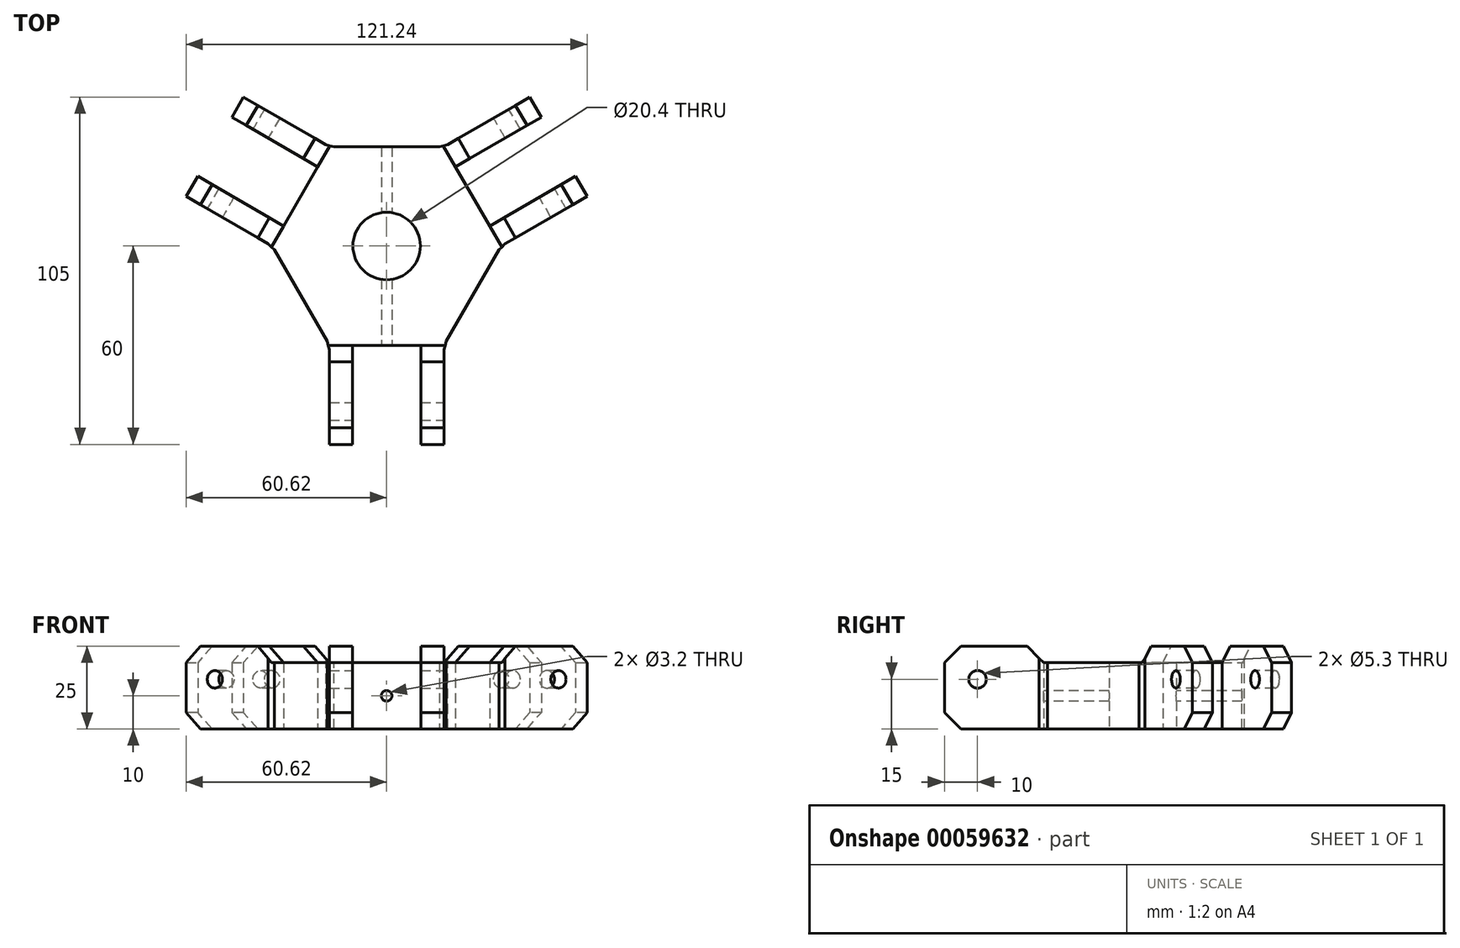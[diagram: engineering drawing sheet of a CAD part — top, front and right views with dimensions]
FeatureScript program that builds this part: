
annotation { "Feature Type Name" : "Feature", "Feature Type Description" : "" }
export const myFeature = defineFeature(function(context is Context, id is Id, definition is map)
    precondition{}
    {
        {
            var Q0;
            Q0=qCreatedBy(makeId("Top.planeOp"),FACE);
            var sketch = newSketch(context, id + "F0", { "sketchPlane" : qUnion([Q0])});
            skLineSegment(sketch, "E0.0", {"start": v(-17.32, 30) * mm, "end": v(17.32, 30) * mm});
            skLineSegment(sketch, "E0.1", {"start": v(17.32, 30) * mm, "end": v(34.64, 0) * mm});
            skLineSegment(sketch, "E0.2", {"start": v(34.64, 0) * mm, "end": v(17.32, -30) * mm});
            skLineSegment(sketch, "E0.3", {"start": v(17.32, -30) * mm, "end": v(-17.32, -30) * mm});
            skLineSegment(sketch, "E0.4", {"start": v(-17.32, -30) * mm, "end": v(-34.64, 0) * mm});
            skLineSegment(sketch, "E0.5", {"start": v(-34.64, 0) * mm, "end": v(-17.32, 30) * mm});
            skLineSegment(sketch, "E1", {"start": v(-34.64, 0) * mm, "end": v(-60.62, 15) * mm});
            skLineSegment(sketch, "E2", {"start": v(-60.62, 15) * mm, "end": v(-57.12, 21.06) * mm});
            skLineSegment(sketch, "E3", {"start": v(-43.3, 45) * mm, "end": v(-17.32, 30) * mm});
            skLineSegment(sketch, "E4", {"start": v(-51.96, 30) * mm, "end": v(-25.98, 15) * mm, "construction": true});
            skLineSegment(sketch, "E5", {"start": v(-46.8, 38.94) * mm, "end": v(-20.82, 23.94) * mm});
            skLineSegment(sketch, "E6", {"start": v(-57.12, 21.06) * mm, "end": v(-31.14, 6.06) * mm});
            skLineSegment(sketch, "E7.trimOffspring", {"start": v(-46.8, 38.94) * mm, "end": v(-43.3, 45) * mm});
            skCircle(sketch, "E8", {"center": v(0, 0) * mm, "radius": 34.64 * mm, "construction": true});
            skLineSegment(sketch, "E9.1.0", {"start": v(10.32, -60) * mm, "end": v(10.32, -30) * mm});
            skLineSegment(sketch, "E9.1.1", {"start": v(-10.32, -60) * mm, "end": v(-17.32, -60) * mm});
            skLineSegment(sketch, "E9.1.2", {"start": v(17.32, -60) * mm, "end": v(10.32, -60) * mm});
            skLineSegment(sketch, "E9.1.3", {"start": v(17.32, -30) * mm, "end": v(17.32, -60) * mm});
            skLineSegment(sketch, "E9.1.4", {"start": v(0, -60) * mm, "end": v(0, -30) * mm, "construction": true});
            skLineSegment(sketch, "E9.1.5", {"start": v(-17.32, -60) * mm, "end": v(-17.32, -30) * mm});
            skLineSegment(sketch, "E9.1.6", {"start": v(-10.32, -60) * mm, "end": v(-10.32, -30) * mm});
            skLineSegment(sketch, "E9.2.0", {"start": v(46.8, 38.94) * mm, "end": v(20.82, 23.94) * mm});
            skLineSegment(sketch, "E9.2.1", {"start": v(57.12, 21.06) * mm, "end": v(60.62, 15) * mm});
            skLineSegment(sketch, "E9.2.2", {"start": v(43.3, 45) * mm, "end": v(46.8, 38.94) * mm});
            skLineSegment(sketch, "E9.2.3", {"start": v(17.32, 30) * mm, "end": v(43.3, 45) * mm});
            skLineSegment(sketch, "E9.2.4", {"start": v(51.96, 30) * mm, "end": v(25.98, 15) * mm, "construction": true});
            skLineSegment(sketch, "E9.2.5", {"start": v(60.62, 15) * mm, "end": v(34.64, 0) * mm});
            skLineSegment(sketch, "E9.2.6", {"start": v(57.12, 21.06) * mm, "end": v(31.14, 6.06) * mm});
            skCircle(sketch, "E10", {"center": v(0, 0) * mm, "radius": 10.2 * mm});
            skSolve(sketch);
        }
        {
            var Q0;
            Q0=makeQuery(id+"F2.opExtrude","CAP_FACE",FACE,{"disambiguationData":[OSD([sQuery(id+"F0.wireOp",EDGE,"E0.0"),sQuery(id+"F0.wireOp",EDGE,"E0.1"),sQuery(id+"F0.wireOp",EDGE,"E0.2"),sQuery(id+"F0.wireOp",EDGE,"E0.3"),sQuery(id+"F0.wireOp",EDGE,"E0.4"),sQuery(id+"F0.wireOp",EDGE,"E0.5"),sQuery(id+"F0.wireOp",EDGE,"E1"),sQuery(id+"F0.wireOp",EDGE,"E2"),sQuery(id+"F0.wireOp",EDGE,"E3"),sQuery(id+"F0.wireOp",EDGE,"E5"),sQuery(id+"F0.wireOp",EDGE,"E6"),sQuery(id+"F0.wireOp",EDGE,"E7.trimOffspring"),sQuery(id+"F0.wireOp",EDGE,"E9.1.0"),sQuery(id+"F0.wireOp",EDGE,"E9.1.1"),sQuery(id+"F0.wireOp",EDGE,"E9.1.2"),sQuery(id+"F0.wireOp",EDGE,"E9.1.3"),sQuery(id+"F0.wireOp",EDGE,"E9.1.5"),sQuery(id+"F0.wireOp",EDGE,"E9.1.6"),sQuery(id+"F0.wireOp",EDGE,"E9.2.0"),sQuery(id+"F0.wireOp",EDGE,"E9.2.1"),sQuery(id+"F0.wireOp",EDGE,"E9.2.2"),sQuery(id+"F0.wireOp",EDGE,"E9.2.3"),sQuery(id+"F0.wireOp",EDGE,"E9.2.5"),sQuery(id+"F0.wireOp",EDGE,"E9.2.6")])],"isStart":false});
            var Q1;
            {var subQ3=sQuery(id+"F0.wireOp",EDGE,"E0.0");Q1=makeQuery(id+"F0.imprint","IMPRINT",FACE,{"disambiguationData":[TD([[makeQuery(id+"F0.imprint","IMPRINT",EDGE,{"derivedFrom":subQ3}),-1.0]])]});}
            extrude(context, id + "F1", {"entities" : qUnion([Q0, Q1]), "depth" : 20 * mm});
        }
        {
            var Q0;
            {var subQ0=sQuery(id+"F0.wireOp",EDGE,"E1");Q0=makeQuery(id+"F0.imprint","IMPRINT",FACE,{"disambiguationData":[TD([[makeQuery(id+"F0.imprint","IMPRINT",EDGE,{"derivedFrom":subQ0}),-1.0]])]});}
            var Q1;
            {var subQ0=sQuery(id+"F0.wireOp",EDGE,"E3");Q1=makeQuery(id+"F0.imprint","IMPRINT",FACE,{"disambiguationData":[TD([[makeQuery(id+"F0.imprint","IMPRINT",EDGE,{"derivedFrom":subQ0}),-1.0]])]});}
            var Q2;
            Q2=makeQuery(id+"F0.imprint","IMPRINT",FACE,{"disambiguationData":[TD([[makeQuery(id+"F0.imprint","IMPRINT",EDGE,{"derivedFrom":sQuery(id+"F0.wireOp",EDGE,"E9.1.1")}),-1.0]])]});
            var Q3;
            {var subQ2=sQuery(id+"F0.wireOp",EDGE,"E9.1.0");Q3=makeQuery(id+"F0.imprint","IMPRINT",FACE,{"disambiguationData":[TD([[makeQuery(id+"F0.imprint","IMPRINT",EDGE,{"derivedFrom":subQ2}),-1.0]])]});}
            var Q4;
            Q4=makeQuery(id+"F0.imprint","IMPRINT",FACE,{"disambiguationData":[TD([[makeQuery(id+"F0.imprint","IMPRINT",EDGE,{"derivedFrom":sQuery(id+"F0.wireOp",EDGE,"E9.2.1")}),-1.0]])]});
            var Q5;
            {var subQ2=sQuery(id+"F0.wireOp",EDGE,"E9.2.0");Q5=makeQuery(id+"F0.imprint","IMPRINT",FACE,{"disambiguationData":[TD([[makeQuery(id+"F0.imprint","IMPRINT",EDGE,{"derivedFrom":subQ2}),-1.0]])]});}
            extrude(context, id + "F2", {"entities" : qUnion([Q0, Q1, Q2, Q3, Q4, Q5]), "operationType" : NewBodyOperationType.ADD, "depth" : 25 * mm});
        }
        {
            var Q0;
            Q0=makeQuery(id+"F2.opExtrude","SWEPT_FACE",FACE,{"disambiguationData":[OSD([sQuery(id+"F0.wireOp",EDGE,"E1")])]});
            var sketch = newSketch(context, id + "F3", { "sketchPlane" : qUnion([Q0])});
            skLineSegment(sketch, "E11", {"start": v(-50, 35.3) * mm, "end": v(-50, -5.3) * mm, "construction": true});
            skPoint(sketch, "E12", {"position": v(-50, 15) * mm});
            skSolve(sketch);
        }
        {
            var Q0;
            Q0=makeQuery(id+"F2.opExtrude","SWEPT_FACE",FACE,{"disambiguationData":[OSD([sQuery(id+"F0.wireOp",EDGE,"E9.1.3")])]});
            var sketch = newSketch(context, id + "F4", { "sketchPlane" : qUnion([Q0])});
            skLineSegment(sketch, "E13", {"start": v(-50, 30.69) * mm, "end": v(-50, -0.69) * mm, "construction": true});
            skPoint(sketch, "E14", {"position": v(-50, 15) * mm});
            skSolve(sketch);
        }
        {
            var Q0;
            Q0=makeQuery(id+"F2.opExtrude","SWEPT_FACE",FACE,{"disambiguationData":[OSD([sQuery(id+"F0.wireOp",EDGE,"E9.2.3")])]});
            var sketch = newSketch(context, id + "F5", { "sketchPlane" : qUnion([Q0])});
            skLineSegment(sketch, "E15", {"start": v(-50, 35.3) * mm, "end": v(-50, -5.3) * mm, "construction": true});
            skPoint(sketch, "E16", {"position": v(-50, 15) * mm});
            skSolve(sketch);
        }
        {
            var Q0;
            Q0=sQuery(id+"F3.wireOp",VERTEX,"E12");
            var Q1;
            Q1=sQuery(id+"F4.wireOp",VERTEX,"E14");
            var Q2;
            Q2=sQuery(id+"F5.wireOp",VERTEX,"E16");
            var Q3;
            Q3=makeQuery(id+"F1.opExtrude","SWEPT_BODY",BODY,{"disambiguationData":[OSD([sQuery(id+"F0.wireOp",EDGE,"E0.0"),sQuery(id+"F0.wireOp",EDGE,"E0.1"),sQuery(id+"F0.wireOp",EDGE,"E0.2"),sQuery(id+"F0.wireOp",EDGE,"E0.3"),sQuery(id+"F0.wireOp",EDGE,"E0.4"),sQuery(id+"F0.wireOp",EDGE,"E0.5")])]});
            hole(context, id + "F6", {"style" : HoleStyle.SIMPLE, "holeDiameter" : 5.3 * mm, "endStyle" : HoleEndStyle.THROUGH, "locations" : qUnion([Q0, Q1, Q2]), "scope" : qUnion([Q3])});
        }
        {
            var Q0;
            Q0=makeQuery(id+"F2.opExtrude","CAP_EDGE",EDGE,{"disambiguationData":[OSD([sQuery(id+"F0.wireOp",EDGE,"E7.trimOffspring")])],"isStart":false});
            var Q1;
            {var subQ0=sQuery(id+"F0.wireOp",EDGE,"E0.3");Q1=makeQuery(id+"F2.opExtrude","CAP_EDGE",EDGE,{"disambiguationData":[OSD([subQ0]),TDD([makeQuery(id+"F0.imprint","IMPRINT",EDGE,{"disambiguationData":[TD([[makeQuery(id+"F0.imprint","INTERSECT",VERTEX,{"derivedFrom":[subQ0,sQuery(id+"F0.wireOp",EDGE,"E9.1.0")]}),1.0]])],"derivedFrom":subQ0})])],"isStart":false});}
            var Q2;
            {var subQ0=sQuery(id+"F0.wireOp",EDGE,"E0.3");Q2=makeQuery(id+"F2.opExtrude","CAP_EDGE",EDGE,{"disambiguationData":[OSD([subQ0]),TDD([makeQuery(id+"F0.imprint","IMPRINT",EDGE,{"disambiguationData":[TD([[makeQuery(id+"F0.imprint","INTERSECT",VERTEX,{"derivedFrom":[subQ0,sQuery(id+"F0.wireOp",EDGE,"E9.1.6")]}),-1.0]])],"derivedFrom":subQ0})])],"isStart":false});}
            var Q3;
            {var subQ0=sQuery(id+"F0.wireOp",EDGE,"E0.5");Q3=makeQuery(id+"F2.opExtrude","CAP_EDGE",EDGE,{"disambiguationData":[OSD([subQ0]),TDD([makeQuery(id+"F0.imprint","IMPRINT",EDGE,{"disambiguationData":[TD([[makeQuery(id+"F0.imprint","INTERSECT",VERTEX,{"derivedFrom":[subQ0,sQuery(id+"F0.wireOp",EDGE,"E6")]}),1.0]])],"derivedFrom":subQ0})])],"isStart":false});}
            var Q4;
            {var subQ0=sQuery(id+"F0.wireOp",EDGE,"E0.5");Q4=makeQuery(id+"F2.opExtrude","CAP_EDGE",EDGE,{"disambiguationData":[OSD([subQ0]),TDD([makeQuery(id+"F0.imprint","IMPRINT",EDGE,{"disambiguationData":[TD([[makeQuery(id+"F0.imprint","INTERSECT",VERTEX,{"derivedFrom":[subQ0,sQuery(id+"F0.wireOp",EDGE,"E5")]}),-1.0]])],"derivedFrom":subQ0})])],"isStart":false});}
            var Q5;
            {var subQ0=sQuery(id+"F0.wireOp",EDGE,"E0.1");Q5=makeQuery(id+"F2.opExtrude","CAP_EDGE",EDGE,{"disambiguationData":[OSD([subQ0]),TDD([makeQuery(id+"F0.imprint","IMPRINT",EDGE,{"disambiguationData":[TD([[makeQuery(id+"F0.imprint","INTERSECT",VERTEX,{"derivedFrom":[subQ0,sQuery(id+"F0.wireOp",EDGE,"E9.2.0")]}),1.0]])],"derivedFrom":subQ0})])],"isStart":false});}
            var Q6;
            {var subQ0=sQuery(id+"F0.wireOp",EDGE,"E0.1");Q6=makeQuery(id+"F2.opExtrude","CAP_EDGE",EDGE,{"disambiguationData":[OSD([subQ0]),TDD([makeQuery(id+"F0.imprint","IMPRINT",EDGE,{"disambiguationData":[TD([[makeQuery(id+"F0.imprint","INTERSECT",VERTEX,{"derivedFrom":[subQ0,sQuery(id+"F0.wireOp",EDGE,"E9.2.6")]}),-1.0]])],"derivedFrom":subQ0})])],"isStart":false});}
            var Q7;
            Q7=makeQuery(id+"F2.opExtrude","CAP_EDGE",EDGE,{"disambiguationData":[OSD([sQuery(id+"F0.wireOp",EDGE,"E7.trimOffspring")])],"isStart":true});
            var Q8;
            Q8=makeQuery(id+"F2.opExtrude","CAP_EDGE",EDGE,{"disambiguationData":[OSD([sQuery(id+"F0.wireOp",EDGE,"E2")])],"isStart":true});
            var Q9;
            Q9=makeQuery(id+"F2.opExtrude","CAP_EDGE",EDGE,{"disambiguationData":[OSD([sQuery(id+"F0.wireOp",EDGE,"E2")])],"isStart":false});
            var Q10;
            Q10=makeQuery(id+"F2.opExtrude","CAP_EDGE",EDGE,{"disambiguationData":[OSD([sQuery(id+"F0.wireOp",EDGE,"E9.1.1")])],"isStart":false});
            var Q11;
            Q11=makeQuery(id+"F2.opExtrude","CAP_EDGE",EDGE,{"disambiguationData":[OSD([sQuery(id+"F0.wireOp",EDGE,"E9.1.2")])],"isStart":false});
            var Q12;
            Q12=makeQuery(id+"F2.opExtrude","CAP_EDGE",EDGE,{"disambiguationData":[OSD([sQuery(id+"F0.wireOp",EDGE,"E9.1.2")])],"isStart":true});
            var Q13;
            Q13=makeQuery(id+"F2.opExtrude","CAP_EDGE",EDGE,{"disambiguationData":[OSD([sQuery(id+"F0.wireOp",EDGE,"E9.1.1")])],"isStart":true});
            var Q14;
            Q14=makeQuery(id+"F2.opExtrude","CAP_EDGE",EDGE,{"disambiguationData":[OSD([sQuery(id+"F0.wireOp",EDGE,"E9.2.1")])],"isStart":false});
            var Q15;
            Q15=makeQuery(id+"F2.opExtrude","CAP_EDGE",EDGE,{"disambiguationData":[OSD([sQuery(id+"F0.wireOp",EDGE,"E9.2.1")])],"isStart":true});
            var Q16;
            Q16=makeQuery(id+"F2.opExtrude","CAP_EDGE",EDGE,{"disambiguationData":[OSD([sQuery(id+"F0.wireOp",EDGE,"E9.2.2")])],"isStart":true});
            var Q17;
            Q17=makeQuery(id+"F2.opExtrude","CAP_EDGE",EDGE,{"disambiguationData":[OSD([sQuery(id+"F0.wireOp",EDGE,"E9.2.2")])],"isStart":false});
            chamfer(context, id + "F7", {"entities" : qUnion([Q0, Q1, Q2, Q3, Q4, Q5, Q6, Q7, Q8, Q9, Q10, Q11, Q12, Q13, Q14, Q15, Q16, Q17]), "width" : 5 * mm, "tangentPropagation" : true});
        }
        {
            var Q0;
            {var subQ1=sQuery(id+"F0.wireOp",EDGE,"E9.1.6");var subQ3=sQuery(id+"F0.wireOp",EDGE,"E0.3");var subQ5=sQuery(id+"F0.wireOp",EDGE,"E0.1");Q0=makeQuery(id+"F2.boolean.opBoolean","SPLIT",EDGE,{"disambiguationData":[TD([makeQuery(id+"F2.opExtrude","CAP_FACE",FACE,{"disambiguationData":[OSD([subQ5,sQuery(id+"F0.wireOp",EDGE,"E9.2.0"),sQuery(id+"F0.wireOp",EDGE,"E9.2.2"),sQuery(id+"F0.wireOp",EDGE,"E9.2.3")])],"isStart":true})])],"derivedFrom":makeQuery(id+"F2.opExtrude","SWEPT_EDGE",EDGE,{"disambiguationData":[OSD([subQ3,subQ1])]})});}
            var Q1;
            {var subQ1=sQuery(id+"F0.wireOp",EDGE,"E0.3");var subQ3=sQuery(id+"F0.wireOp",EDGE,"E9.1.0");var subQ4=sQuery(id+"F0.wireOp",EDGE,"E0.1");Q1=makeQuery(id+"F2.boolean.opBoolean","SPLIT",EDGE,{"disambiguationData":[TD([makeQuery(id+"F2.opExtrude","CAP_FACE",FACE,{"disambiguationData":[OSD([subQ4,sQuery(id+"F0.wireOp",EDGE,"E9.2.0"),sQuery(id+"F0.wireOp",EDGE,"E9.2.2"),sQuery(id+"F0.wireOp",EDGE,"E9.2.3")])],"isStart":true})])],"derivedFrom":makeQuery(id+"F2.opExtrude","SWEPT_EDGE",EDGE,{"disambiguationData":[OSD([subQ1,subQ3])]})});}
            var Q2;
            {var subQ0=sQuery(id+"F0.wireOp",EDGE,"E9.1.3");var subQ1=sQuery(id+"F0.wireOp",EDGE,"E0.3");var subQ2=sQuery(id+"F0.wireOp",EDGE,"E0.2");Q2=makeQuery(id+"F2.boolean.opBoolean","MERGE",EDGE,{"derivedFrom":[makeQuery(id+"F1.opExtrude","SWEPT_EDGE",EDGE,{"disambiguationData":[OSD([subQ2,subQ1,subQ0])]}),makeQuery(id+"F2.opExtrude","SWEPT_EDGE",EDGE,{"disambiguationData":[OSD([subQ2,subQ1,subQ0])]})]});}
            var Q3;
            {var subQ0=sQuery(id+"F0.wireOp",EDGE,"E9.2.5");var subQ1=sQuery(id+"F0.wireOp",EDGE,"E0.2");var subQ2=sQuery(id+"F0.wireOp",EDGE,"E0.1");Q3=makeQuery(id+"F2.boolean.opBoolean","MERGE",EDGE,{"derivedFrom":[makeQuery(id+"F1.opExtrude","SWEPT_EDGE",EDGE,{"disambiguationData":[OSD([subQ2,subQ1,subQ0])]}),makeQuery(id+"F2.opExtrude","SWEPT_EDGE",EDGE,{"disambiguationData":[OSD([subQ2,subQ1,subQ0])]})]});}
            var Q4;
            {var subQ2=sQuery(id+"F0.wireOp",EDGE,"E9.2.6");var subQ4=sQuery(id+"F0.wireOp",EDGE,"E0.1");Q4=makeQuery(id+"F2.boolean.opBoolean","SPLIT",EDGE,{"disambiguationData":[TD([makeQuery(id+"F2.opExtrude","CAP_FACE",FACE,{"disambiguationData":[OSD([subQ4,sQuery(id+"F0.wireOp",EDGE,"E9.2.0"),sQuery(id+"F0.wireOp",EDGE,"E9.2.2"),sQuery(id+"F0.wireOp",EDGE,"E9.2.3")])],"isStart":true})])],"derivedFrom":makeQuery(id+"F2.opExtrude","SWEPT_EDGE",EDGE,{"disambiguationData":[OSD([subQ4,subQ2])]})});}
            var Q5;
            {var subQ2=sQuery(id+"F0.wireOp",EDGE,"E0.1");var subQ7=sQuery(id+"F0.wireOp",EDGE,"E9.2.3");var subQ8=sQuery(id+"F0.wireOp",EDGE,"E9.2.0");Q5=makeQuery(id+"F2.boolean.opBoolean","SPLIT",EDGE,{"disambiguationData":[TD([makeQuery(id+"F2.opExtrude","CAP_FACE",FACE,{"disambiguationData":[OSD([subQ2,subQ8,sQuery(id+"F0.wireOp",EDGE,"E9.2.2"),subQ7])],"isStart":true})])],"derivedFrom":makeQuery(id+"F2.opExtrude","SWEPT_EDGE",EDGE,{"disambiguationData":[OSD([subQ2,subQ8])]})});}
            var Q6;
            {var subQ0=sQuery(id+"F0.wireOp",EDGE,"E9.2.3");var subQ1=sQuery(id+"F0.wireOp",EDGE,"E0.1");var subQ2=sQuery(id+"F0.wireOp",EDGE,"E0.0");Q6=makeQuery(id+"F2.boolean.opBoolean","MERGE",EDGE,{"derivedFrom":[makeQuery(id+"F1.opExtrude","SWEPT_EDGE",EDGE,{"disambiguationData":[OSD([subQ2,subQ1,subQ0])]}),makeQuery(id+"F2.opExtrude","SWEPT_EDGE",EDGE,{"disambiguationData":[OSD([subQ2,subQ1,subQ0])]})]});}
            var Q7;
            {var subQ0=sQuery(id+"F0.wireOp",EDGE,"E3");var subQ1=sQuery(id+"F0.wireOp",EDGE,"E0.5");var subQ2=sQuery(id+"F0.wireOp",EDGE,"E0.0");Q7=makeQuery(id+"F2.boolean.opBoolean","MERGE",EDGE,{"derivedFrom":[makeQuery(id+"F1.opExtrude","SWEPT_EDGE",EDGE,{"disambiguationData":[OSD([subQ2,subQ1,subQ0])]}),makeQuery(id+"F2.opExtrude","SWEPT_EDGE",EDGE,{"disambiguationData":[OSD([subQ2,subQ1,subQ0])]})]});}
            var Q8;
            {var subQ1=sQuery(id+"F0.wireOp",EDGE,"E0.5");var subQ3=sQuery(id+"F0.wireOp",EDGE,"E5");var subQ8=sQuery(id+"F0.wireOp",EDGE,"E0.1");Q8=makeQuery(id+"F2.boolean.opBoolean","SPLIT",EDGE,{"disambiguationData":[TD([makeQuery(id+"F2.opExtrude","CAP_FACE",FACE,{"disambiguationData":[OSD([subQ8,sQuery(id+"F0.wireOp",EDGE,"E9.2.0"),sQuery(id+"F0.wireOp",EDGE,"E9.2.2"),sQuery(id+"F0.wireOp",EDGE,"E9.2.3")])],"isStart":true})])],"derivedFrom":makeQuery(id+"F2.opExtrude","SWEPT_EDGE",EDGE,{"disambiguationData":[OSD([subQ1,subQ3])]})});}
            var Q9;
            {var subQ0=sQuery(id+"F0.wireOp",EDGE,"E6");var subQ2=sQuery(id+"F0.wireOp",EDGE,"E0.5");var subQ7=sQuery(id+"F0.wireOp",EDGE,"E0.1");Q9=makeQuery(id+"F2.boolean.opBoolean","SPLIT",EDGE,{"disambiguationData":[TD([makeQuery(id+"F2.opExtrude","CAP_FACE",FACE,{"disambiguationData":[OSD([subQ7,sQuery(id+"F0.wireOp",EDGE,"E9.2.0"),sQuery(id+"F0.wireOp",EDGE,"E9.2.2"),sQuery(id+"F0.wireOp",EDGE,"E9.2.3")])],"isStart":true})])],"derivedFrom":makeQuery(id+"F2.opExtrude","SWEPT_EDGE",EDGE,{"disambiguationData":[OSD([subQ2,subQ0])]})});}
            var Q10;
            {var subQ0=sQuery(id+"F0.wireOp",EDGE,"E1");var subQ1=sQuery(id+"F0.wireOp",EDGE,"E0.5");var subQ2=sQuery(id+"F0.wireOp",EDGE,"E0.4");Q10=makeQuery(id+"F2.boolean.opBoolean","MERGE",EDGE,{"derivedFrom":[makeQuery(id+"F1.opExtrude","SWEPT_EDGE",EDGE,{"disambiguationData":[OSD([subQ2,subQ1,subQ0])]}),makeQuery(id+"F2.opExtrude","SWEPT_EDGE",EDGE,{"disambiguationData":[OSD([subQ2,subQ1,subQ0])]})]});}
            var Q11;
            {var subQ0=sQuery(id+"F0.wireOp",EDGE,"E9.1.5");var subQ1=sQuery(id+"F0.wireOp",EDGE,"E0.4");var subQ2=sQuery(id+"F0.wireOp",EDGE,"E0.3");Q11=makeQuery(id+"F2.boolean.opBoolean","MERGE",EDGE,{"derivedFrom":[makeQuery(id+"F1.opExtrude","SWEPT_EDGE",EDGE,{"disambiguationData":[OSD([subQ2,subQ1,subQ0])]}),makeQuery(id+"F2.opExtrude","SWEPT_EDGE",EDGE,{"disambiguationData":[OSD([subQ2,subQ1,subQ0])]})]});}
            chamfer(context, id + "F8", {"entities" : qUnion([Q0, Q1, Q2, Q3, Q4, Q5, Q6, Q7, Q8, Q9, Q10, Q11]), "width" : 5 * mm, "tangentPropagation" : true});
        }
        {
            var Q0;
            Q0=makeQuery(id+"F1.opExtrude","SWEPT_FACE",FACE,{"disambiguationData":[OSD([sQuery(id+"F0.wireOp",EDGE,"E0.3")])]});
            var sketch = newSketch(context, id + "F9", { "sketchPlane" : qUnion([Q0])});
            skLineSegment(sketch, "E17", {"start": v(-5.32, 20) * mm, "end": v(5.32, 0) * mm, "construction": true});
            skLineSegment(sketch, "E18", {"start": v(-5.32, 0) * mm, "end": v(5.32, 20) * mm, "construction": true});
            skPoint(sketch, "E19", {"position": v(0, 10) * mm});
            skSolve(sketch);
        }
        {
            var Q0;
            Q0=sQuery(id+"F9.wireOp",VERTEX,"E19");
            var Q1;
            Q1=makeQuery(id+"F1.opExtrude","SWEPT_BODY",BODY,{"disambiguationData":[OSD([sQuery(id+"F0.wireOp",EDGE,"E0.0"),sQuery(id+"F0.wireOp",EDGE,"E0.1"),sQuery(id+"F0.wireOp",EDGE,"E0.2"),sQuery(id+"F0.wireOp",EDGE,"E0.3"),sQuery(id+"F0.wireOp",EDGE,"E0.4"),sQuery(id+"F0.wireOp",EDGE,"E0.5"),sQuery(id+"F0.wireOp",EDGE,"E10")])]});
            hole(context, id + "F10", {"style" : HoleStyle.SIMPLE, "endStyle" : HoleEndStyle.THROUGH, "holeDiameter" : 3.2 * mm, "locations" : qUnion([Q0]), "scope" : qUnion([Q1]), "isTappedThrough" : true});
        }
    });
